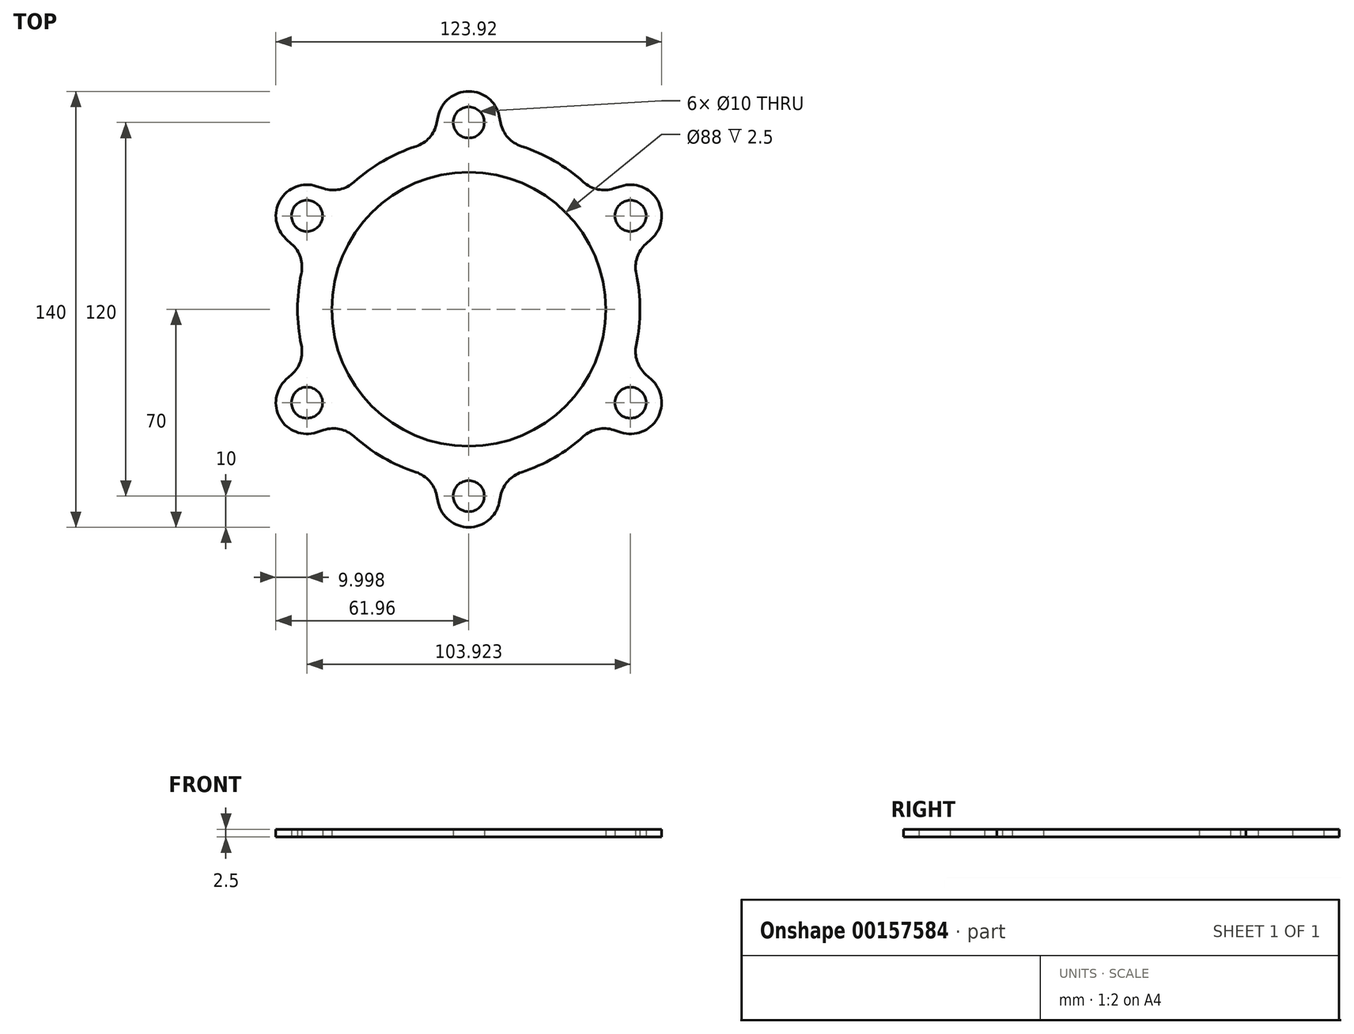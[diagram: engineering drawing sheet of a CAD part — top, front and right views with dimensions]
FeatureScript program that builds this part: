
annotation { "Feature Type Name" : "Feature", "Feature Type Description" : "" }
export const myFeature = defineFeature(function(context is Context, id is Id, definition is map)
    precondition{}
    {
        {
            var Q0;
            Q0=qCreatedBy(makeId("Top.planeOp"),FACE);
            var sketch = newSketch(context, id + "F0", { "sketchPlane" : qUnion([Q0])});
            skCircle(sketch, "E0", {"center": v(0, 0) * mm, "radius": 44 * mm});
            skCircle(sketch, "E1", {"center": v(0, 0) * mm, "radius": 55 * mm});
            skCircle(sketch, "E2", {"center": v(0, 0) * mm, "radius": 60 * mm, "construction": true});
            skCircle(sketch, "E3", {"center": v(0, 60) * mm, "radius": 5 * mm});
            skArc(sketch, "E4.0", {"start": v(9.78, 62.08) * mm, "mid": v(0, 70) * mm, "end": v(-9.78, 62.08) * mm});
            skCircle(sketch, "E5", {"center": v(0, 0) * mm, "radius": 22.5 * mm, "construction": true});
            skLineSegment(sketch, "E6.trimOffspring", {"start": v(-11.55, 53.77) * mm, "end": v(-9.78, 62.08) * mm});
            skLineSegment(sketch, "E7.trimOffspring", {"start": v(11.55, 53.77) * mm, "end": v(9.78, 62.08) * mm});
            skArc(sketch, "E8.1.0", {"start": v(-48.88, 39.51) * mm, "mid": v(-60.62, 35) * mm, "end": v(-58.66, 22.57) * mm});
            skLineSegment(sketch, "E8.1.1", {"start": v(-52.34, 16.88) * mm, "end": v(-58.66, 22.57) * mm});
            skLineSegment(sketch, "E8.1.2", {"start": v(-40.8, 36.89) * mm, "end": v(-48.88, 39.51) * mm});
            skCircle(sketch, "E8.1.3", {"center": v(-51.96, 30) * mm, "radius": 5 * mm});
            skArc(sketch, "E8.2.0", {"start": v(-58.66, -22.57) * mm, "mid": v(-60.62, -35) * mm, "end": v(-48.88, -39.51) * mm});
            skLineSegment(sketch, "E8.2.1", {"start": v(-40.8, -36.89) * mm, "end": v(-48.88, -39.51) * mm});
            skLineSegment(sketch, "E8.2.2", {"start": v(-52.34, -16.88) * mm, "end": v(-58.66, -22.57) * mm});
            skCircle(sketch, "E8.2.3", {"center": v(-51.96, -30) * mm, "radius": 5 * mm});
            skArc(sketch, "E8.3.0", {"start": v(-9.78, -62.08) * mm, "mid": v(0, -70) * mm, "end": v(9.78, -62.08) * mm});
            skLineSegment(sketch, "E8.3.1", {"start": v(11.55, -53.77) * mm, "end": v(9.78, -62.08) * mm});
            skLineSegment(sketch, "E8.3.2", {"start": v(-11.55, -53.77) * mm, "end": v(-9.78, -62.08) * mm});
            skCircle(sketch, "E8.3.3", {"center": v(0, -60) * mm, "radius": 5 * mm});
            skArc(sketch, "E8.4.0", {"start": v(48.88, -39.51) * mm, "mid": v(60.62, -35) * mm, "end": v(58.66, -22.57) * mm});
            skLineSegment(sketch, "E8.4.1", {"start": v(52.34, -16.88) * mm, "end": v(58.66, -22.57) * mm});
            skLineSegment(sketch, "E8.4.2", {"start": v(40.8, -36.89) * mm, "end": v(48.88, -39.51) * mm});
            skCircle(sketch, "E8.4.3", {"center": v(51.96, -30) * mm, "radius": 5 * mm});
            skArc(sketch, "E8.5.0", {"start": v(58.66, 22.57) * mm, "mid": v(60.62, 35) * mm, "end": v(48.88, 39.51) * mm});
            skLineSegment(sketch, "E8.5.1", {"start": v(40.8, 36.89) * mm, "end": v(48.88, 39.51) * mm});
            skLineSegment(sketch, "E8.5.2", {"start": v(52.34, 16.88) * mm, "end": v(58.66, 22.57) * mm});
            skCircle(sketch, "E8.5.3", {"center": v(51.96, 30) * mm, "radius": 5 * mm});
            skSolve(sketch);
        }
        {
            var Q0;
            Q0=makeQuery(id+"F0.imprint","IMPRINT",FACE,{"disambiguationData":[TD([[makeQuery(id+"F0.imprint","IMPRINT",EDGE,{"derivedFrom":sQuery(id+"F0.wireOp",EDGE,"E0")}),-1.0]])]});
            var Q1;
            {var subQ2=sQuery(id+"F0.wireOp",EDGE,"E3");Q1=makeQuery(id+"F0.imprint","IMPRINT",FACE,{"disambiguationData":[TD([[makeQuery(id+"F0.imprint","IMPRINT",EDGE,{"derivedFrom":subQ2}),-1.0]])]});}
            var Q2;
            {var subQ2=sQuery(id+"F0.wireOp",EDGE,"1db648ab-f3a5-4f71-9374-6c022d9bd438.5.0");Q2=makeQuery(id+"F0.imprint","IMPRINT",FACE,{"disambiguationData":[TD([[makeQuery(id+"F0.imprint","IMPRINT",EDGE,{"derivedFrom":subQ2}),-1.0]])]});}
            var Q3;
            {var subQ2=sQuery(id+"F0.wireOp",EDGE,"1db648ab-f3a5-4f71-9374-6c022d9bd438.4.0");Q3=makeQuery(id+"F0.imprint","IMPRINT",FACE,{"disambiguationData":[TD([[makeQuery(id+"F0.imprint","IMPRINT",EDGE,{"derivedFrom":subQ2}),-1.0]])]});}
            var Q4;
            {var subQ2=sQuery(id+"F0.wireOp",EDGE,"1db648ab-f3a5-4f71-9374-6c022d9bd438.3.0");Q4=makeQuery(id+"F0.imprint","IMPRINT",FACE,{"disambiguationData":[TD([[makeQuery(id+"F0.imprint","IMPRINT",EDGE,{"derivedFrom":subQ2}),-1.0]])]});}
            var Q5;
            {var subQ2=sQuery(id+"F0.wireOp",EDGE,"1db648ab-f3a5-4f71-9374-6c022d9bd438.2.0");Q5=makeQuery(id+"F0.imprint","IMPRINT",FACE,{"disambiguationData":[TD([[makeQuery(id+"F0.imprint","IMPRINT",EDGE,{"derivedFrom":subQ2}),-1.0]])]});}
            var Q6;
            {var subQ2=sQuery(id+"F0.wireOp",EDGE,"1db648ab-f3a5-4f71-9374-6c022d9bd438.1.0");Q6=makeQuery(id+"F0.imprint","IMPRINT",FACE,{"disambiguationData":[TD([[makeQuery(id+"F0.imprint","IMPRINT",EDGE,{"derivedFrom":subQ2}),-1.0]])]});}
            var Q7;
            Q7=makeQuery(id+"F0.imprint","IMPRINT",FACE,{"disambiguationData":[TD([[makeQuery(id+"F0.imprint","IMPRINT",EDGE,{"derivedFrom":sQuery(id+"F0.wireOp",EDGE,"E8.1.0")}),1.0]])]});
            var Q8;
            Q8=makeQuery(id+"F0.imprint","IMPRINT",FACE,{"disambiguationData":[TD([[makeQuery(id+"F0.imprint","IMPRINT",EDGE,{"derivedFrom":sQuery(id+"F0.wireOp",EDGE,"E8.2.0")}),1.0]])]});
            var Q9;
            Q9=makeQuery(id+"F0.imprint","IMPRINT",FACE,{"disambiguationData":[TD([[makeQuery(id+"F0.imprint","IMPRINT",EDGE,{"derivedFrom":sQuery(id+"F0.wireOp",EDGE,"E8.3.0")}),1.0]])]});
            var Q10;
            Q10=makeQuery(id+"F0.imprint","IMPRINT",FACE,{"disambiguationData":[TD([[makeQuery(id+"F0.imprint","IMPRINT",EDGE,{"derivedFrom":sQuery(id+"F0.wireOp",EDGE,"E8.4.0")}),1.0]])]});
            var Q11;
            Q11=makeQuery(id+"F0.imprint","IMPRINT",FACE,{"disambiguationData":[TD([[makeQuery(id+"F0.imprint","IMPRINT",EDGE,{"derivedFrom":sQuery(id+"F0.wireOp",EDGE,"E8.5.0")}),1.0]])]});
            extrude(context, id + "F1", {"entities" : qUnion([Q0, Q1, Q2, Q3, Q4, Q5, Q6, Q7, Q8, Q9, Q10, Q11]), "depth" : 2.5 * mm});
        }
        {
            var Q0;
            Q0=makeQuery(id+"F1.opExtrude","SWEPT_EDGE",EDGE,{"disambiguationData":[OSD([sQuery(id+"F0.wireOp",EDGE,"E1"),sQuery(id+"F0.wireOp",EDGE,"E8.4.1")])]});
            var Q1;
            Q1=makeQuery(id+"F1.opExtrude","SWEPT_EDGE",EDGE,{"disambiguationData":[OSD([sQuery(id+"F0.wireOp",EDGE,"E1"),sQuery(id+"F0.wireOp",EDGE,"E8.5.2")])]});
            var Q2;
            Q2=makeQuery(id+"F1.opExtrude","SWEPT_EDGE",EDGE,{"disambiguationData":[OSD([sQuery(id+"F0.wireOp",EDGE,"E1"),sQuery(id+"F0.wireOp",EDGE,"E8.5.1")])]});
            var Q3;
            Q3=makeQuery(id+"F1.opExtrude","SWEPT_EDGE",EDGE,{"disambiguationData":[OSD([sQuery(id+"F0.wireOp",EDGE,"E1"),sQuery(id+"F0.wireOp",EDGE,"E7.trimOffspring")])]});
            var Q4;
            Q4=makeQuery(id+"F1.opExtrude","SWEPT_EDGE",EDGE,{"disambiguationData":[OSD([sQuery(id+"F0.wireOp",EDGE,"E1"),sQuery(id+"F0.wireOp",EDGE,"E6.trimOffspring")])]});
            var Q5;
            Q5=makeQuery(id+"F1.opExtrude","SWEPT_EDGE",EDGE,{"disambiguationData":[OSD([sQuery(id+"F0.wireOp",EDGE,"E1"),sQuery(id+"F0.wireOp",EDGE,"E8.1.2")])]});
            var Q6;
            Q6=makeQuery(id+"F1.opExtrude","SWEPT_EDGE",EDGE,{"disambiguationData":[OSD([sQuery(id+"F0.wireOp",EDGE,"E1"),sQuery(id+"F0.wireOp",EDGE,"E8.1.1")])]});
            var Q7;
            Q7=makeQuery(id+"F1.opExtrude","SWEPT_EDGE",EDGE,{"disambiguationData":[OSD([sQuery(id+"F0.wireOp",EDGE,"E1"),sQuery(id+"F0.wireOp",EDGE,"E8.2.2")])]});
            var Q8;
            Q8=makeQuery(id+"F1.opExtrude","SWEPT_EDGE",EDGE,{"disambiguationData":[OSD([sQuery(id+"F0.wireOp",EDGE,"E1"),sQuery(id+"F0.wireOp",EDGE,"E8.2.1")])]});
            var Q9;
            Q9=makeQuery(id+"F1.opExtrude","SWEPT_EDGE",EDGE,{"disambiguationData":[OSD([sQuery(id+"F0.wireOp",EDGE,"E1"),sQuery(id+"F0.wireOp",EDGE,"E8.3.2")])]});
            var Q10;
            Q10=makeQuery(id+"F1.opExtrude","SWEPT_EDGE",EDGE,{"disambiguationData":[OSD([sQuery(id+"F0.wireOp",EDGE,"E1"),sQuery(id+"F0.wireOp",EDGE,"E8.3.1")])]});
            var Q11;
            Q11=makeQuery(id+"F1.opExtrude","SWEPT_EDGE",EDGE,{"disambiguationData":[OSD([sQuery(id+"F0.wireOp",EDGE,"E1"),sQuery(id+"F0.wireOp",EDGE,"E8.4.2")])]});
            fillet(context, id + "F2", {"entities" : qUnion([Q0, Q1, Q2, Q3, Q4, Q5, Q6, Q7, Q8, Q9, Q10, Q11]), "radius" : 10 * mm, "tangentPropagation" : true, "allowEdgeOverflow" : false});
        }
    });
